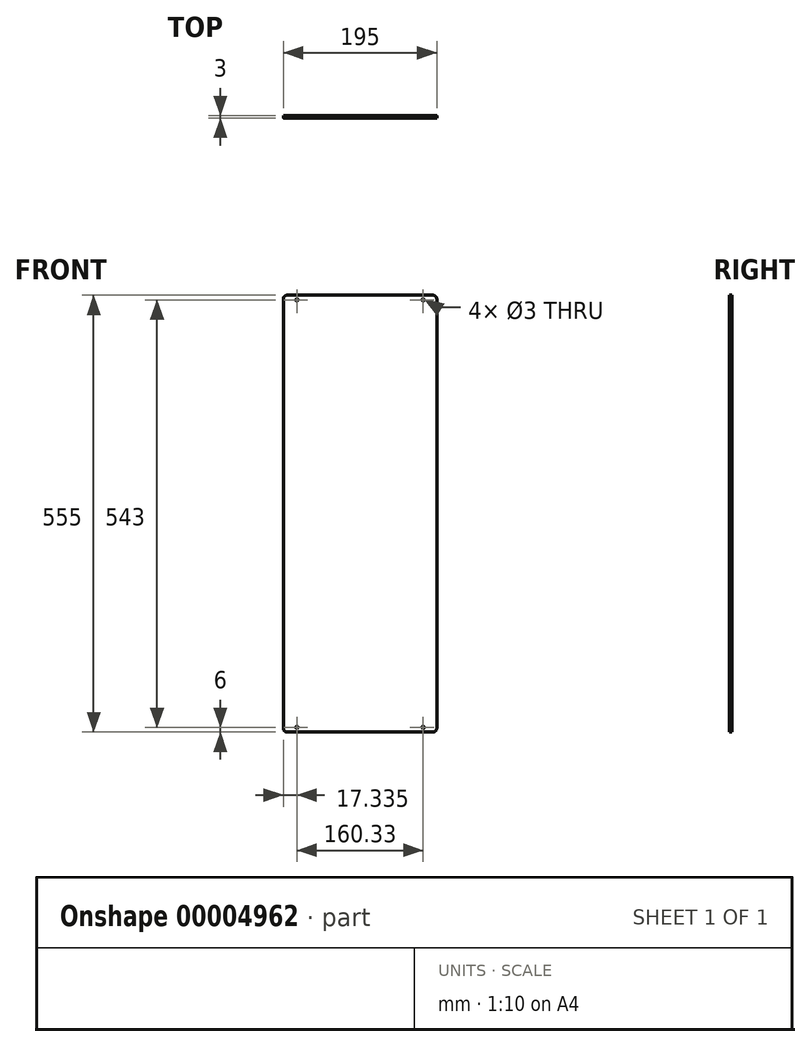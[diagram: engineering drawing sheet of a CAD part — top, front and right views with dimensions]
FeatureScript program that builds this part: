
annotation { "Feature Type Name" : "Feature", "Feature Type Description" : "" }
export const myFeature = defineFeature(function(context is Context, id is Id, definition is map)
    precondition{}
    {
        {
            var Q0;
            Q0=qCreatedBy(makeId("Front.planeOp"),FACE);
            var sketch = newSketch(context, id + "F0", { "sketchPlane" : qUnion([Q0])});
            skLineSegment(sketch, "E0.rect.bottom", {"start": v(97.5, 277.5) * mm, "end": v(-97.5, 277.5) * mm});
            skLineSegment(sketch, "E0.rect.top", {"start": v(97.5, -277.5) * mm, "end": v(-97.5, -277.5) * mm});
            skLineSegment(sketch, "E0.rect.left", {"start": v(97.5, 277.5) * mm, "end": v(97.5, -277.5) * mm});
            skLineSegment(sketch, "E0.rect.right", {"start": v(-97.5, 277.5) * mm, "end": v(-97.5, -277.5) * mm});
            skPoint(sketch, "E0.rect.middle", {"position": v(0, 0) * mm});
            skLineSegment(sketch, "E1", {"start": v(0, 277.5) * mm, "end": v(0, -277.5) * mm, "construction": true});
            skLineSegment(sketch, "E2", {"start": v(0, 0) * mm, "end": v(97.5, 0) * mm, "construction": true});
            skCircle(sketch, "E3", {"center": v(80.17, 271.5) * mm, "radius": 1.5 * mm});
            skCircle(sketch, "E4.0.MirrorC", {"center": v(80.17, -271.5) * mm, "radius": 1.5 * mm});
            skCircle(sketch, "E5.0.MirrorC", {"center": v(-80.17, -271.5) * mm, "radius": 1.5 * mm});
            skCircle(sketch, "E5.1.MirrorC", {"center": v(-80.17, 271.5) * mm, "radius": 1.5 * mm});
            skSolve(sketch);
        }
        {
            var Q0;
            Q0 = qSketchRegion(id + "F0", true);
            extrude(context, id + "F1", {"entities" : qUnion([Q0]), "depth" : 3 * mm});
        }
        {
            var Q0;
            Q0=makeQuery(id+"F1.opExtrude","SWEPT_EDGE",EDGE,{"disambiguationData":[OSD([sQuery(id+"F0.wireOp",EDGE,"E0.rect.bottom"),sQuery(id+"F0.wireOp",EDGE,"E0.rect.left")])]});
            var Q1;
            Q1=makeQuery(id+"F1.opExtrude","SWEPT_EDGE",EDGE,{"disambiguationData":[OSD([sQuery(id+"F0.wireOp",EDGE,"E0.rect.bottom"),sQuery(id+"F0.wireOp",EDGE,"E0.rect.right")])]});
            var Q2;
            Q2=makeQuery(id+"F1.opExtrude","SWEPT_EDGE",EDGE,{"disambiguationData":[OSD([sQuery(id+"F0.wireOp",EDGE,"E0.rect.top"),sQuery(id+"F0.wireOp",EDGE,"E0.rect.left")])]});
            var Q3;
            Q3=makeQuery(id+"F1.opExtrude","SWEPT_EDGE",EDGE,{"disambiguationData":[OSD([sQuery(id+"F0.wireOp",EDGE,"E0.rect.top"),sQuery(id+"F0.wireOp",EDGE,"E0.rect.right")])]});
            fillet(context, id + "F2", {"entities" : qUnion([Q0, Q1, Q2, Q3]), "radius" : 5 * mm, "tangentPropagation" : true, "allowEdgeOverflow" : false});
        }
    });
